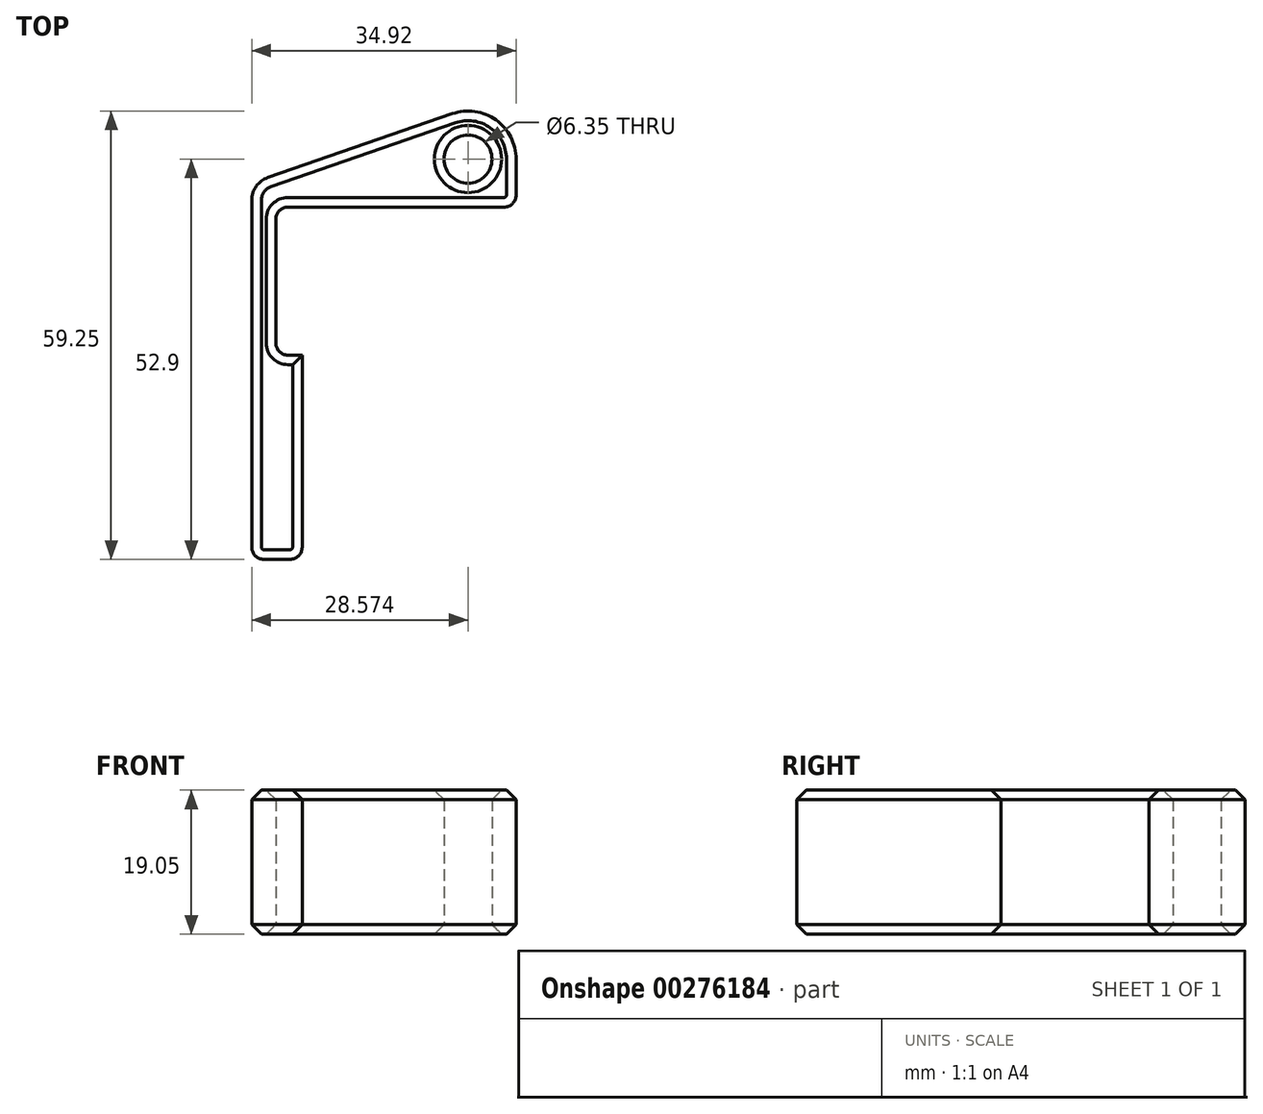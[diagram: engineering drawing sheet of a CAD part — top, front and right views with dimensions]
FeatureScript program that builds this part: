
annotation { "Feature Type Name" : "Feature", "Feature Type Description" : "" }
export const myFeature = defineFeature(function(context is Context, id is Id, definition is map)
    precondition{}
    {
        {
            var Q0;
            Q0=qCreatedBy(makeId("Top.planeOp"),FACE);
            var sketch = newSketch(context, id + "F0", { "sketchPlane" : qUnion([Q0])});
            skLineSegment(sketch, "E0", {"start": v(14.36, 28.6) * mm, "end": v(14.36, 44.96) * mm});
            skLineSegment(sketch, "E1", {"start": v(15.95, 46.55) * mm, "end": v(39.76, 46.55) * mm});
            skLineSegment(sketch, "E2", {"start": v(11.19, 47.46) * mm, "end": v(11.19, 1.6) * mm});
            skLineSegment(sketch, "E3.bottom", {"start": v(15.96, 27) * mm, "end": v(17.84, 27) * mm});
            skLineSegment(sketch, "E3.right", {"start": v(17.84, 27) * mm, "end": v(17.84, 1.6) * mm});
            skArc(sketch, "E4", {"start": v(46.11, 52.9) * mm, "mid": v(43.45, 58.07) * mm, "end": v(37.69, 58.9) * mm});
            skLineSegment(sketch, "E5", {"start": v(12.79, 0) * mm, "end": v(16.24, 0) * mm});
            skLineSegment(sketch, "E6", {"start": v(13.33, 50.46) * mm, "end": v(37.69, 58.9) * mm});
            skPoint(sketch, "E7.visualSharp", {"position": v(14.36, 46.55) * mm});
            skArc(sketch, "E7.filletArc", {"start": v(15.95, 46.55) * mm, "mid": v(14.83, 46.09) * mm, "end": v(14.36, 44.96) * mm});
            skPoint(sketch, "E8.visualSharp", {"position": v(11.19, 49.73) * mm});
            skArc(sketch, "E8.filletArc", {"start": v(13.33, 50.46) * mm, "mid": v(11.78, 49.3) * mm, "end": v(11.19, 47.46) * mm});
            skPoint(sketch, "E9.visualSharp", {"position": v(14.36, 27) * mm});
            skArc(sketch, "E9.filletArc", {"start": v(14.36, 28.6) * mm, "mid": v(14.83, 27.47) * mm, "end": v(15.96, 27) * mm});
            skPoint(sketch, "E10.visualSharp", {"position": v(17.84, 0) * mm});
            skArc(sketch, "E10.filletArc", {"start": v(16.24, 0) * mm, "mid": v(17.38, 0.47) * mm, "end": v(17.84, 1.6) * mm});
            skPoint(sketch, "E11.visualSharp", {"position": v(11.19, 0) * mm});
            skArc(sketch, "E11.filletArc", {"start": v(11.19, 1.6) * mm, "mid": v(11.66, 0.47) * mm, "end": v(12.79, 0) * mm});
            skCircle(sketch, "E12", {"center": v(39.76, 52.9) * mm, "radius": 3.18 * mm});
            skLineSegment(sketch, "E13", {"start": v(46.11, 52.9) * mm, "end": v(46.11, 48.15) * mm});
            skLineSegment(sketch, "E14", {"start": v(44.51, 46.55) * mm, "end": v(39.76, 46.55) * mm});
            skPoint(sketch, "E15.visualSharp", {"position": v(46.11, 46.55) * mm});
            skArc(sketch, "E15.filletArc", {"start": v(44.51, 46.55) * mm, "mid": v(45.65, 47.02) * mm, "end": v(46.11, 48.15) * mm});
            skSolve(sketch);
        }
        {
            var Q0;
            Q0 = qSketchRegion(id + "F0", true);
            extrude(context, id + "F1", {"entities" : qUnion([Q0]), "depth" : 19.05 * mm});
        }
        {
            var Q0;
            Q0=makeQuery(id+"F1.opExtrude","CAP_EDGE",EDGE,{"disambiguationData":[OSD([sQuery(id+"F0.wireOp",EDGE,"E6")])],"isStart":false});
            var Q1;
            Q1=makeQuery(id+"F1.opExtrude","CAP_EDGE",EDGE,{"disambiguationData":[OSD([sQuery(id+"F0.wireOp",EDGE,"E12")])],"isStart":false});
            var Q2;
            Q2=makeQuery(id+"F1.opExtrude","CAP_EDGE",EDGE,{"disambiguationData":[OSD([sQuery(id+"F0.wireOp",EDGE,"E1"),sQuery(id+"F0.wireOp",EDGE,"E14")])],"isStart":true});
            var Q3;
            Q3=makeQuery(id+"F1.opExtrude","CAP_EDGE",EDGE,{"disambiguationData":[OSD([sQuery(id+"F0.wireOp",EDGE,"E12")])],"isStart":true});
            chamfer(context, id + "F2", {"entities" : qUnion([Q0, Q1, Q2, Q3]), "width" : 1.27 * mm, "tangentPropagation" : true});
        }
    });
